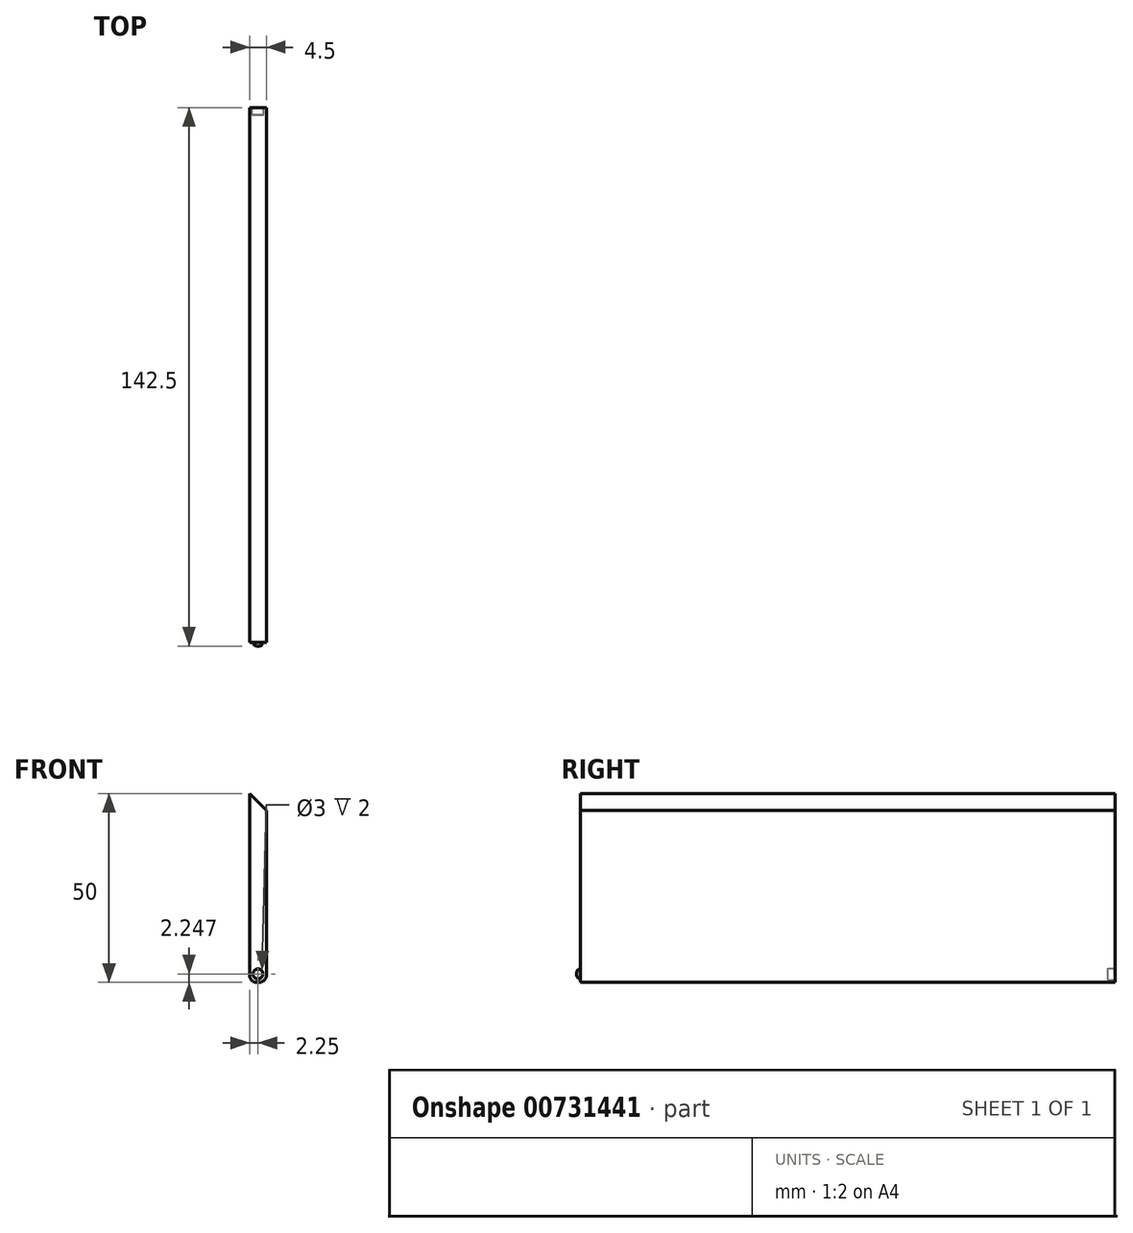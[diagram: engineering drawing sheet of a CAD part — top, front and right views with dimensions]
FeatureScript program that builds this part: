
annotation { "Feature Type Name" : "Feature", "Feature Type Description" : "" }
export const myFeature = defineFeature(function(context is Context, id is Id, definition is map)
    precondition{}
    {
        {
            var Q0;
            Q0=qCreatedBy(makeId("Front.planeOp"),FACE);
            var sketch = newSketch(context, id + "F0", { "sketchPlane" : qUnion([Q0])});
            skLineSegment(sketch, "E0", {"start": v(-4.25, 51.23) * mm, "end": v(0.25, 46.73) * mm});
            skLineSegment(sketch, "E1", {"start": v(0.25, 46.73) * mm, "end": v(0.25, 3.23) * mm});
            skLineSegment(sketch, "E2", {"start": v(-1.75, 1.23) * mm, "end": v(-2.25, 1.23) * mm});
            skLineSegment(sketch, "E3", {"start": v(-4.25, 3.23) * mm, "end": v(-4.25, 51.23) * mm});
            skCircle(sketch, "E4", {"center": v(-2, 3.48) * mm, "radius": 1.5 * mm});
            skCircle(sketch, "E5", {"center": v(-2, 3.48) * mm, "radius": 1.3 * mm});
            skPoint(sketch, "E6.visualSharp", {"position": v(0.25, 1.23) * mm});
            skArc(sketch, "E6.filletArc", {"start": v(-1.75, 1.23) * mm, "mid": v(-0.34, 1.81) * mm, "end": v(0.25, 3.23) * mm});
            skPoint(sketch, "E7.visualSharp", {"position": v(-4.25, 1.23) * mm});
            skArc(sketch, "E7.filletArc", {"start": v(-4.25, 3.23) * mm, "mid": v(-3.66, 1.81) * mm, "end": v(-2.25, 1.23) * mm});
            skSolve(sketch);
        }
        {
            var Q0;
            Q0=makeQuery(id+"F0.imprint","IMPRINT",FACE,{"disambiguationData":[TD([[makeQuery(id+"F0.imprint","IMPRINT",EDGE,{"derivedFrom":sQuery(id+"F0.wireOp",EDGE,"E0")}),-1.0]])]});
            extrude(context, id + "F1", {"entities" : qUnion([Q0]), "depth" : 141.5 * mm, "offsetDistance" : 25 * mm});
        }
        {
            var Q0;
            Q0=makeQuery(id+"F0.imprint","IMPRINT",FACE,{"disambiguationData":[TD([[makeQuery(id+"F0.imprint","IMPRINT",EDGE,{"derivedFrom":sQuery(id+"F0.wireOp",EDGE,"E4")}),1.0]])]});
            extrude(context, id + "F2", {"entities" : qUnion([Q0]), "operationType" : NewBodyOperationType.ADD, "depth" : 141.5 * mm, "offsetDistance" : 25 * mm});
        }
        {
            var Q0;
            Q0=makeQuery(id+"F0.imprint","IMPRINT",FACE,{"disambiguationData":[TD([[makeQuery(id+"F0.imprint","IMPRINT",EDGE,{"derivedFrom":sQuery(id+"F0.wireOp",EDGE,"E5")}),1.0]])]});
            extrude(context, id + "F3", {"entities" : qUnion([Q0]), "operationType" : NewBodyOperationType.ADD, "depth" : 142.5 * mm, "offsetDistance" : 25 * mm});
        }
        {
            var Q0;
            Q0=makeQuery(id+"F0.imprint","IMPRINT",FACE,{"disambiguationData":[TD([[makeQuery(id+"F0.imprint","IMPRINT",EDGE,{"derivedFrom":sQuery(id+"F0.wireOp",EDGE,"E4")}),1.0]])]});
            var Q1;
            Q1=makeQuery(id+"F0.imprint","IMPRINT",FACE,{"disambiguationData":[TD([[makeQuery(id+"F0.imprint","IMPRINT",EDGE,{"derivedFrom":sQuery(id+"F0.wireOp",EDGE,"E5")}),1.0]])]});
            extrude(context, id + "F4", {"entities" : qUnion([Q0, Q1]), "operationType" : NewBodyOperationType.REMOVE, "depth" : 2 * mm, "offsetDistance" : 25 * mm});
        }
        {
            var Q0;
            Q0=makeQuery(id+"F3.opExtrude","CAP_EDGE",EDGE,{"disambiguationData":[OSD([sQuery(id+"F0.wireOp",EDGE,"E5")])],"isStart":false});
            fillet(context, id + "F5", {"entities" : qUnion([Q0]), "radius" : 1 * mm, "tangentPropagation" : true, "allowEdgeOverflow" : false});
        }
    });
